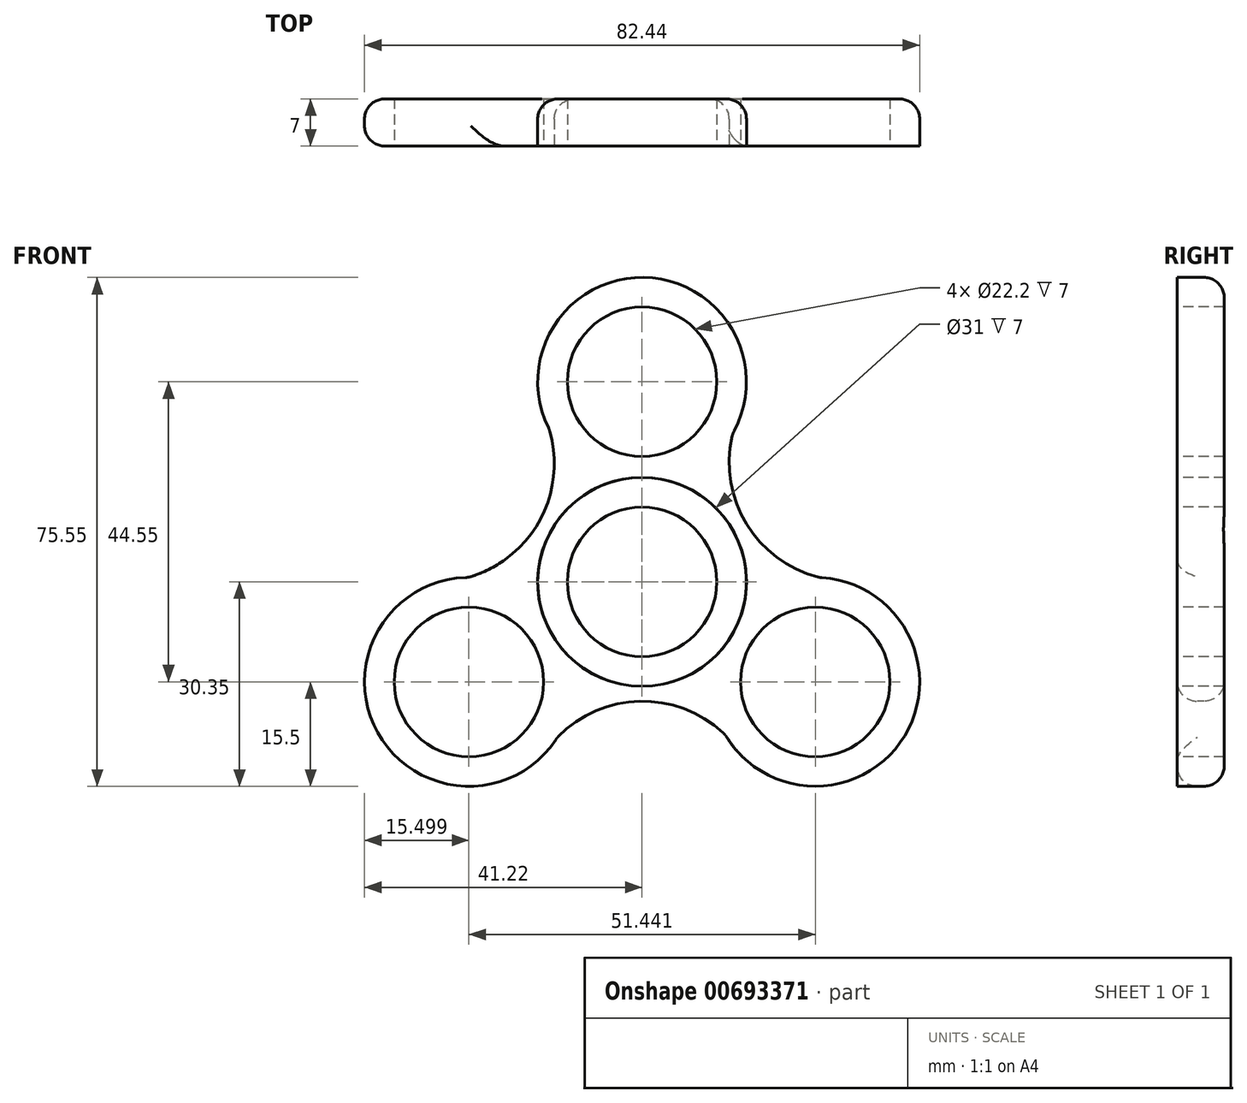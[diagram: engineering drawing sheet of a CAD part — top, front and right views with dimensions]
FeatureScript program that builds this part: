
annotation { "Feature Type Name" : "Feature", "Feature Type Description" : "" }
export const myFeature = defineFeature(function(context is Context, id is Id, definition is map)
    precondition{}
    {
        {
            var Q0;
            Q0=qCreatedBy(makeId("Front.planeOp"),FACE);
            var sketch = newSketch(context, id + "F0", { "sketchPlane" : qUnion([Q0])});
            skCircle(sketch, "E0", {"center": v(0, 0) * mm, "radius": 15.5 * mm});
            skCircle(sketch, "E1", {"center": v(0, 0) * mm, "radius": 11.1 * mm});
            skCircle(sketch, "E2", {"center": v(0, 29.7) * mm, "radius": 15.5 * mm});
            skCircle(sketch, "E3", {"center": v(0, 29.7) * mm, "radius": 11.1 * mm});
            skCircle(sketch, "E4.1.0", {"center": v(-25.72, -14.85) * mm, "radius": 11.1 * mm});
            skCircle(sketch, "E4.1.1", {"center": v(-25.72, -14.85) * mm, "radius": 15.5 * mm});
            skCircle(sketch, "E4.2.0", {"center": v(25.72, -14.85) * mm, "radius": 11.1 * mm});
            skCircle(sketch, "E4.2.1", {"center": v(25.72, -14.85) * mm, "radius": 15.5 * mm});
            skArc(sketch, "E5", {"start": v(-30.16, 0) * mm, "mid": v(-15.55, 8.52) * mm, "end": v(-14.9, 25.42) * mm});
            skArc(sketch, "E6.1.0", {"start": v(15.08, -26.12) * mm, "mid": v(0.4, -17.72) * mm, "end": v(-14.57, -25.61) * mm});
            skArc(sketch, "E6.2.0", {"start": v(15.08, 26.12) * mm, "mid": v(15.15, 9.2) * mm, "end": v(29.47, 0.2) * mm});
            skSolve(sketch);
        }
        {
            var Q0;
            Q0 = qSketchRegion(id + "F0", true);
            extrude(context, id + "F1", {"entities" : qUnion([Q0]), "oppositeDirection" : true, "depth" : 7 * mm, "offsetDistance" : 25 * mm});
        }
        {
            var Q0;
            Q0=qCreatedBy(makeId("Front.planeOp"),FACE);
            var sketch = newSketch(context, id + "F2", { "sketchPlane" : qUnion([Q0])});
            skCircle(sketch, "E7", {"center": v(0, 0) * mm, "radius": 11.1 * mm});
            skCircle(sketch, "E8", {"center": v(0, 0) * mm, "radius": 15.5 * mm});
            skSolve(sketch);
        }
        {
            var Q0;
            Q0=makeQuery(id+"F2.imprint","IMPRINT",FACE,{"disambiguationData":[TD([[makeQuery(id+"F2.imprint","IMPRINT",EDGE,{"derivedFrom":sQuery(id+"F2.wireOp",EDGE,"E7")}),-1.0]])]});
            extrude(context, id + "F3", {"entities" : qUnion([Q0]), "oppositeDirection" : true, "depth" : 7 * mm, "offsetDistance" : 25 * mm});
        }
        {
            var Q0;
            Q0=makeQuery(id+"F1.opExtrude","CAP_EDGE",EDGE,{"disambiguationData":[OSD([sQuery(id+"F0.wireOp",EDGE,"E6.1.0")])],"isStart":true});
            var Q1;
            Q1=makeQuery(id+"F1.opExtrude","SWEPT_EDGE",EDGE,{"disambiguationData":[OSD([sQuery(id+"F0.wireOp",EDGE,"E4.2.1"),sQuery(id+"F0.wireOp",EDGE,"E6.1.0")])]});
            var Q2;
            Q2=makeQuery(id+"F1.opExtrude","CAP_EDGE",EDGE,{"disambiguationData":[OSD([sQuery(id+"F0.wireOp",EDGE,"E4.1.1")])],"isStart":true});
            var Q3;
            Q3=makeQuery(id+"F1.opExtrude","SWEPT_EDGE",EDGE,{"disambiguationData":[OSD([sQuery(id+"F0.wireOp",EDGE,"E4.1.1"),sQuery(id+"F0.wireOp",EDGE,"E6.1.0")])]});
            var Q4;
            Q4=makeQuery(id+"F1.opExtrude","SWEPT_EDGE",EDGE,{"disambiguationData":[OSD([sQuery(id+"F0.wireOp",EDGE,"E4.1.1"),sQuery(id+"F0.wireOp",EDGE,"E5")])]});
            var Q5;
            Q5=makeQuery(id+"F1.opExtrude","SWEPT_EDGE",EDGE,{"disambiguationData":[OSD([sQuery(id+"F0.wireOp",EDGE,"E2"),sQuery(id+"F0.wireOp",EDGE,"E5")])]});
            var Q6;
            Q6=makeQuery(id+"F1.opExtrude","SWEPT_EDGE",EDGE,{"disambiguationData":[OSD([sQuery(id+"F0.wireOp",EDGE,"E2"),sQuery(id+"F0.wireOp",EDGE,"E6.2.0")])]});
            var Q7;
            Q7=makeQuery(id+"F1.opExtrude","SWEPT_EDGE",EDGE,{"disambiguationData":[OSD([sQuery(id+"F0.wireOp",EDGE,"E4.2.1"),sQuery(id+"F0.wireOp",EDGE,"E6.2.0")])]});
            fillet(context, id + "F4", {"entities" : qUnion([Q0, Q1, Q2, Q3, Q4, Q5, Q6, Q7]), "radius" : 3 * mm, "tangentPropagation" : true, "allowEdgeOverflow" : false});
        }
        {
            var Q0;
            Q0=makeQuery(id+"F1.opExtrude","CAP_EDGE",EDGE,{"disambiguationData":[OSD([sQuery(id+"F0.wireOp",EDGE,"E6.2.0")])],"isStart":false});
            fillet(context, id + "F5", {"entities" : qUnion([Q0]), "radius" : 3 * mm, "tangentPropagation" : true, "allowEdgeOverflow" : false});
        }
    });
